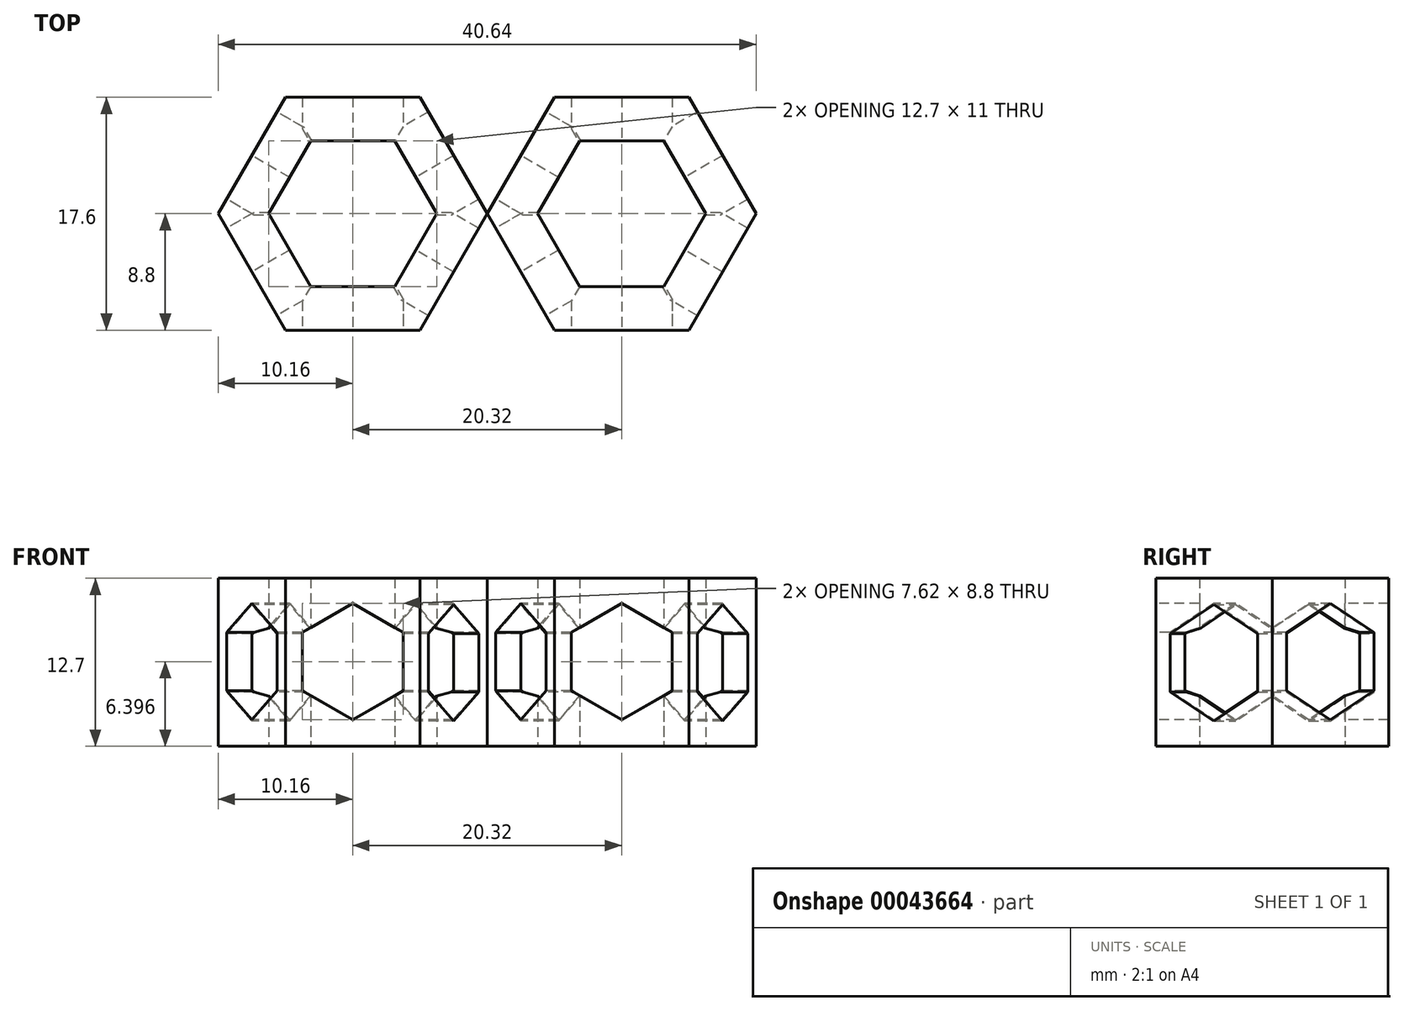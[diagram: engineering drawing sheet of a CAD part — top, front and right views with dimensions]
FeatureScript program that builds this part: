
annotation { "Feature Type Name" : "Feature", "Feature Type Description" : "" }
export const myFeature = defineFeature(function(context is Context, id is Id, definition is map)
    precondition{}
    {
        {
            var Q0;
            Q0=qCreatedBy(makeId("Top.planeOp"),FACE);
            var sketch = newSketch(context, id + "F0", { "sketchPlane" : qUnion([Q0])});
            skCircle(sketch, "E0.cCircle", {"center": v(0, 0) * mm, "radius": 5.5 * mm, "construction": true});
            skLineSegment(sketch, "E0.0", {"start": v(-3.17, 5.5) * mm, "end": v(3.17, 5.5) * mm});
            skLineSegment(sketch, "E0.1", {"start": v(3.17, 5.5) * mm, "end": v(6.35, 0) * mm});
            skLineSegment(sketch, "E0.2", {"start": v(6.35, 0) * mm, "end": v(3.18, -5.5) * mm});
            skLineSegment(sketch, "E0.3", {"start": v(3.18, -5.5) * mm, "end": v(-3.17, -5.5) * mm});
            skLineSegment(sketch, "E0.4", {"start": v(-3.17, -5.5) * mm, "end": v(-6.35, 0) * mm});
            skLineSegment(sketch, "E0.5", {"start": v(-6.35, 0) * mm, "end": v(-3.17, 5.5) * mm});
            skPoint(sketch, "E0.0.midPoint", {"position": v(0, 5.5) * mm});
            skSolve(sketch);
        }
        {
            var Q0;
            Q0=makeQuery(id+"F0.imprint","IMPRINT",FACE,{"disambiguationData":[TD([[makeQuery(id+"F0.imprint","IMPRINT",EDGE,{"derivedFrom":sQuery(id+"F0.wireOp",EDGE,"E0.0")}),-1.0]])]});
            var sketch = newSketch(context, id + "F1", { "sketchPlane" : qUnion([Q0])});
            skCircle(sketch, "E1.cCircle", {"center": v(0, 0) * mm, "radius": 8.8 * mm, "construction": true});
            skLineSegment(sketch, "E1.0", {"start": v(-5.08, 8.8) * mm, "end": v(5.08, 8.8) * mm});
            skLineSegment(sketch, "E1.1", {"start": v(5.08, 8.8) * mm, "end": v(10.16, 0) * mm});
            skLineSegment(sketch, "E1.2", {"start": v(10.16, 0) * mm, "end": v(5.08, -8.8) * mm});
            skLineSegment(sketch, "E1.3", {"start": v(5.08, -8.8) * mm, "end": v(-5.08, -8.8) * mm});
            skLineSegment(sketch, "E1.4", {"start": v(-5.08, -8.8) * mm, "end": v(-10.16, 0) * mm});
            skLineSegment(sketch, "E1.5", {"start": v(-10.16, 0) * mm, "end": v(-5.08, 8.8) * mm});
            skPoint(sketch, "E1.0.midPoint", {"position": v(0, 8.8) * mm});
            skSolve(sketch);
        }
        {
            var Q0;
            Q0=makeQuery(id+"F1.imprint","IMPRINT",FACE,{"disambiguationData":[TD([[makeQuery(id+"F1.imprint","IMPRINT",EDGE,{"derivedFrom":sQuery(id+"F1.wireOp",EDGE,"E1.0")}),1.0]])]});
            var Q1;
            Q1=makeQuery(id+"F1.imprint","IMPRINT",FACE,{"disambiguationData":[TD([[makeQuery(id+"F1.imprint","IMPRINT",EDGE,{"derivedFrom":sQuery(id+"F1.wireOp",EDGE,"E1.0")}),-1.0]])]});
            extrude(context, id + "F2", {"entities" : qUnion([Q0, Q1]), "depth" : 12.7 * mm});
        }
        {
            var Q0;
            Q0=makeQuery(id+"F2.opExtrude","SWEPT_FACE",FACE,{"disambiguationData":[OSD([sQuery(id+"F0.wireOp",EDGE,"E0.4")])]});
            var sketch = newSketch(context, id + "F3", { "sketchPlane" : qUnion([Q0])});
            skCircle(sketch, "E2.cCircle", {"center": v(0, -1.69) * mm, "radius": 0.64 * mm, "construction": true});
            skLineSegment(sketch, "E2.0", {"start": v(0.64, -1.32) * mm, "end": v(0.64, -2.05) * mm});
            skLineSegment(sketch, "E2.1", {"start": v(0.64, -2.05) * mm, "end": v(0, -2.42) * mm});
            skLineSegment(sketch, "E2.2", {"start": v(0, -2.42) * mm, "end": v(-0.64, -2.05) * mm});
            skLineSegment(sketch, "E2.3", {"start": v(-0.63, -2.05) * mm, "end": v(-0.63, -1.32) * mm});
            skLineSegment(sketch, "E2.4", {"start": v(-0.63, -1.32) * mm, "end": v(0, -0.95) * mm});
            skLineSegment(sketch, "E2.5", {"start": v(0, -0.95) * mm, "end": v(0.64, -1.32) * mm});
            skPoint(sketch, "E2.0.midPoint", {"position": v(0.64, -1.69) * mm});
            skSolve(sketch);
        }
        {
            var Q0;
            Q0=makeQuery(id+"F3.imprint","IMPRINT",FACE,{"disambiguationData":[TD([[makeQuery(id+"F3.imprint","IMPRINT",EDGE,{"derivedFrom":sQuery(id+"F3.wireOp",EDGE,"E2.0")}),-1.0]])]});
            extrude(context, id + "F4", {"entities" : qUnion([Q0]), "operationType" : NewBodyOperationType.REMOVE, "oppositeDirection" : true, "depth" : 50.8 * mm});
        }
        {
            var Q0;
            Q0=makeQuery(id+"F2.opExtrude","SWEPT_FACE",FACE,{"disambiguationData":[OSD([sQuery(id+"F1.wireOp",EDGE,"E1.5")])]});
            var sketch = newSketch(context, id + "F5", { "sketchPlane" : qUnion([Q0])});
            skCircle(sketch, "E3.cCircle", {"center": v(0, 6.3) * mm, "radius": 3.81 * mm, "construction": true});
            skLineSegment(sketch, "E3.0", {"start": v(3.81, 4.1) * mm, "end": v(0, 1.9) * mm});
            skLineSegment(sketch, "E3.1", {"start": v(0, 1.9) * mm, "end": v(-3.81, 4.1) * mm});
            skLineSegment(sketch, "E3.2", {"start": v(-3.81, 4.1) * mm, "end": v(-3.81, 8.5) * mm});
            skLineSegment(sketch, "E3.3", {"start": v(-3.81, 8.5) * mm, "end": v(0, 10.7) * mm});
            skLineSegment(sketch, "E3.4", {"start": v(0, 10.7) * mm, "end": v(3.81, 8.5) * mm});
            skLineSegment(sketch, "E3.5", {"start": v(3.81, 8.5) * mm, "end": v(3.81, 4.1) * mm});
            skPoint(sketch, "E3.0.midPoint", {"position": v(1.9, 3) * mm});
            skSolve(sketch);
        }
        {
            var Q0;
            Q0=makeQuery(id+"F5.imprint","IMPRINT",FACE,{"disambiguationData":[TD([[makeQuery(id+"F5.imprint","IMPRINT",EDGE,{"derivedFrom":sQuery(id+"F5.wireOp",EDGE,"E3.0")}),-1.0]])]});
            extrude(context, id + "F6", {"entities" : qUnion([Q0]), "operationType" : NewBodyOperationType.REMOVE, "oppositeDirection" : true, "depth" : 25.4 * mm});
        }
        {
            var Q0;
            Q0=makeQuery(id+"F2.opExtrude","SWEPT_FACE",FACE,{"disambiguationData":[OSD([sQuery(id+"F1.wireOp",EDGE,"E1.4")])]});
            var sketch = newSketch(context, id + "F7", { "sketchPlane" : qUnion([Q0])});
            skCircle(sketch, "E4.cCircle", {"center": v(0, 6.4) * mm, "radius": 3.81 * mm, "construction": true});
            skLineSegment(sketch, "E4.0", {"start": v(0, 10.8) * mm, "end": v(3.81, 8.6) * mm});
            skLineSegment(sketch, "E4.1", {"start": v(3.8, 8.6) * mm, "end": v(3.8, 4.2) * mm});
            skLineSegment(sketch, "E4.2", {"start": v(3.8, 4.2) * mm, "end": v(0, 2) * mm});
            skLineSegment(sketch, "E4.3", {"start": v(0, 2) * mm, "end": v(-3.81, 4.2) * mm});
            skLineSegment(sketch, "E4.4", {"start": v(-3.81, 4.2) * mm, "end": v(-3.81, 8.6) * mm});
            skLineSegment(sketch, "E4.5", {"start": v(-3.81, 8.6) * mm, "end": v(0, 10.8) * mm});
            skPoint(sketch, "E4.0.midPoint", {"position": v(1.9, 9.7) * mm});
            skSolve(sketch);
        }
        {
            var Q0;
            Q0=makeQuery(id+"F7.imprint","IMPRINT",FACE,{"disambiguationData":[TD([[makeQuery(id+"F7.imprint","IMPRINT",EDGE,{"derivedFrom":sQuery(id+"F7.wireOp",EDGE,"E4.0")}),-1.0]])]});
            extrude(context, id + "F8", {"entities" : qUnion([Q0]), "operationType" : NewBodyOperationType.REMOVE, "oppositeDirection" : true, "depth" : 50.8 * mm});
        }
        {
            var Q0;
            Q0=makeQuery(id+"F2.opExtrude","SWEPT_FACE",FACE,{"disambiguationData":[OSD([sQuery(id+"F1.wireOp",EDGE,"E1.3")])]});
            var sketch = newSketch(context, id + "F9", { "sketchPlane" : qUnion([Q0])});
            skCircle(sketch, "E5.cCircle", {"center": v(0, 6.4) * mm, "radius": 3.8 * mm, "construction": true});
            skLineSegment(sketch, "E5.0", {"start": v(3.8, 8.6) * mm, "end": v(3.8, 4.2) * mm});
            skLineSegment(sketch, "E5.1", {"start": v(3.8, 4.2) * mm, "end": v(0, 2) * mm});
            skLineSegment(sketch, "E5.2", {"start": v(0, 2) * mm, "end": v(-3.81, 4.2) * mm});
            skLineSegment(sketch, "E5.3", {"start": v(-3.8, 4.2) * mm, "end": v(-3.8, 8.6) * mm});
            skLineSegment(sketch, "E5.4", {"start": v(-3.8, 8.6) * mm, "end": v(0, 10.8) * mm});
            skLineSegment(sketch, "E5.5", {"start": v(0, 10.8) * mm, "end": v(3.81, 8.6) * mm});
            skPoint(sketch, "E5.0.midPoint", {"position": v(3.8, 6.4) * mm});
            skSolve(sketch);
        }
        {
            var Q0;
            Q0=makeQuery(id+"F9.imprint","IMPRINT",FACE,{"disambiguationData":[TD([[makeQuery(id+"F9.imprint","IMPRINT",EDGE,{"derivedFrom":sQuery(id+"F9.wireOp",EDGE,"E5.0")}),-1.0]])]});
            extrude(context, id + "F10", {"entities" : qUnion([Q0]), "operationType" : NewBodyOperationType.REMOVE, "oppositeDirection" : true, "depth" : 50.8 * mm});
        }
        {
            var Q0;
            Q0=makeQuery(id+"F2.opExtrude","SWEPT_BODY",BODY,{"disambiguationData":[OSD([sQuery(id+"F0.wireOp",EDGE,"E0.0"),sQuery(id+"F0.wireOp",EDGE,"E0.1"),sQuery(id+"F0.wireOp",EDGE,"E0.2"),sQuery(id+"F0.wireOp",EDGE,"E0.3"),sQuery(id+"F0.wireOp",EDGE,"E0.4"),sQuery(id+"F0.wireOp",EDGE,"E0.5"),sQuery(id+"F1.wireOp",EDGE,"E1.0"),sQuery(id+"F1.wireOp",EDGE,"E1.1"),sQuery(id+"F1.wireOp",EDGE,"E1.2"),sQuery(id+"F1.wireOp",EDGE,"E1.3"),sQuery(id+"F1.wireOp",EDGE,"E1.4"),sQuery(id+"F1.wireOp",EDGE,"E1.5")])]});
            var Q1;
            Q1=qCreatedBy(makeId("Right.planeOp"),FACE);
            transform(context, id + "F11", {"entities" : qUnion([Q0]), "transformType" : TransformType.TRANSLATION_DISTANCE, "transformDirection" : qUnion([Q1]), "distance" : 20.32 * mm, "makeCopy" : true});
        }
    });
